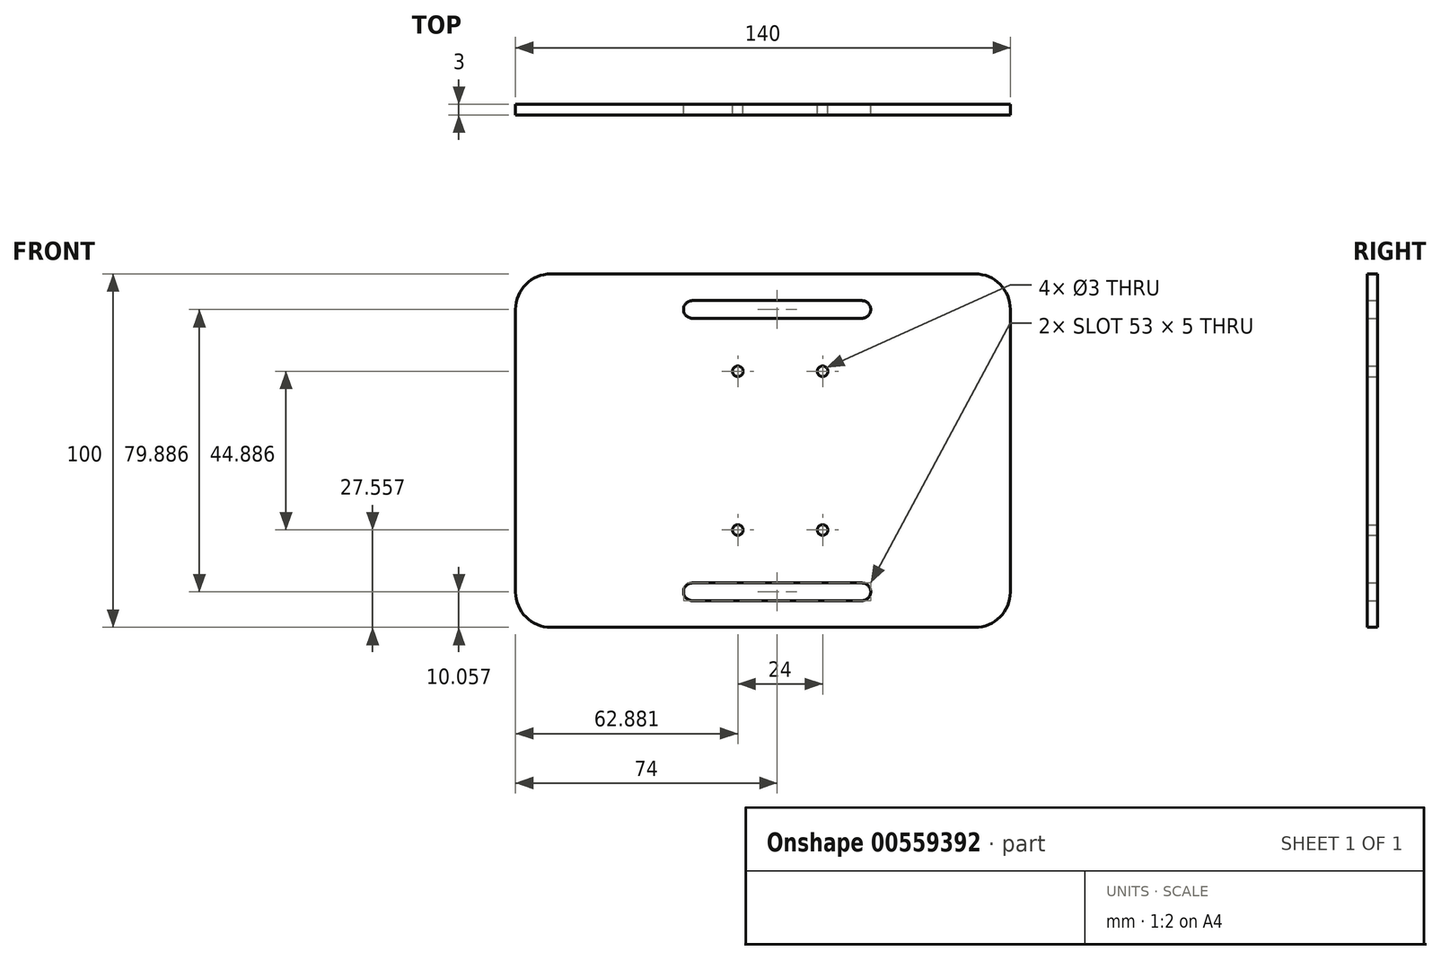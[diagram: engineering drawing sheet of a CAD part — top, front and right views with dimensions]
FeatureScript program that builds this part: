
annotation { "Feature Type Name" : "Feature", "Feature Type Description" : "" }
export const myFeature = defineFeature(function(context is Context, id is Id, definition is map)
    precondition{}
    {
        {
            var Q0;
            Q0=qCreatedBy(makeId("Front.planeOp"),FACE);
            var sketch = newSketch(context, id + "F0", { "sketchPlane" : qUnion([Q0])});
            skLineSegment(sketch, "E0.bottom", {"start": v(-140, 0) * mm, "end": v(0, 0) * mm});
            skLineSegment(sketch, "E0.top", {"start": v(-140, 50) * mm, "end": v(0, 50) * mm});
            skLineSegment(sketch, "E0.left", {"start": v(-140, 0) * mm, "end": v(-140, 50) * mm});
            skLineSegment(sketch, "E0.right", {"start": v(0, 0) * mm, "end": v(0, 50) * mm});
            skSolve(sketch);
        }
        {
            var Q0;
            Q0=qCreatedBy(makeId("Front.planeOp"),FACE);
            var sketch = newSketch(context, id + "F1", { "sketchPlane" : qUnion([Q0])});
            skLineSegment(sketch, "E1", {"start": v(-90, 39.94) * mm, "end": v(-42, 39.94) * mm});
            skArc(sketch, "E2.0.startCap", {"start": v(-90, 37.44) * mm, "mid": v(-92.5, 39.94) * mm, "end": v(-90, 42.44) * mm});
            skArc(sketch, "E2.0.endCap", {"start": v(-42, 42.44) * mm, "mid": v(-39.5, 39.94) * mm, "end": v(-42, 37.44) * mm});
            skLineSegment(sketch, "E2.0.left", {"start": v(-90, 42.44) * mm, "end": v(-42, 42.44) * mm});
            skLineSegment(sketch, "E2.0.right", {"start": v(-90, 37.44) * mm, "end": v(-42, 37.44) * mm});
            skSolve(sketch);
        }
        {
            var Q0;
            Q0=qCreatedBy(makeId("Front.planeOp"),FACE);
            var sketch = newSketch(context, id + "F2", { "sketchPlane" : qUnion([Q0])});
            skLineSegment(sketch, "E3", {"start": v(-77.12, 22.44) * mm, "end": v(-53.12, 22.44) * mm});
            skSolve(sketch);
        }
        {
            var Q0;
            Q0=qCreatedBy(makeId("Front.planeOp"),FACE);
            var sketch = newSketch(context, id + "F3", { "sketchPlane" : qUnion([Q0])});
            skSolve(sketch);
        }
        {
            var Q0;
            Q0=makeQuery(id+"F0.imprint","IMPRINT",FACE,{"disambiguationData":[TD([[makeQuery(id+"F0.imprint","IMPRINT",EDGE,{"derivedFrom":sQuery(id+"F0.wireOp",EDGE,"E0.bottom")}),1.0]])]});
            extrude(context, id + "F4", {"entities" : qUnion([Q0]), "depth" : 3 * mm, "offsetDistance" : 25 * mm});
        }
        {
            var Q0;
            Q0=sQuery(id+"F2.wireOp",VERTEX,"E3.end");
            var Q1;
            Q1=makeQuery(id+"F4.opExtrude","SWEPT_BODY",BODY,{"disambiguationData":[OSD([sQuery(id+"F0.wireOp",EDGE,"E0.bottom"),sQuery(id+"F0.wireOp",EDGE,"E0.top"),sQuery(id+"F0.wireOp",EDGE,"E0.left"),sQuery(id+"F0.wireOp",EDGE,"E0.right")])]});
            hole(context, id + "F5", {"style" : HoleStyle.SIMPLE, "endStyle" : HoleEndStyle.THROUGH, "oppositeDirection" : true, "holeDiameter" : 3 * mm, "isTappedThrough" : true, "tappedDepth" : 12 * mm, "tapClearance" : 3, "locations" : qUnion([Q0]), "scope" : qUnion([Q1])});
        }
        {
            var Q0;
            Q0=sQuery(id+"F2.wireOp",VERTEX,"E3.start");
            var Q1;
            Q1=makeQuery(id+"F4.opExtrude","SWEPT_BODY",BODY,{"disambiguationData":[OSD([sQuery(id+"F0.wireOp",EDGE,"E0.bottom"),sQuery(id+"F0.wireOp",EDGE,"E0.top"),sQuery(id+"F0.wireOp",EDGE,"E0.left"),sQuery(id+"F0.wireOp",EDGE,"E0.right")])]});
            hole(context, id + "F6", {"style" : HoleStyle.SIMPLE, "endStyle" : HoleEndStyle.THROUGH, "oppositeDirection" : true, "holeDiameter" : 3 * mm, "isTappedThrough" : true, "tappedDepth" : 12 * mm, "tapClearance" : 3, "locations" : qUnion([Q0]), "scope" : qUnion([Q1])});
        }
        {
            var Q0;
            Q0 = qSketchRegion(id + "F1", true);
            var sketch = newSketch(context, id + "F7", { "sketchPlane" : qUnion([Q0])});
            skSolve(sketch);
        }
        {
            var Q0;
            Q0 = qSketchRegion(id + "F1", true);
            extrude(context, id + "F8", {"entities" : qUnion([Q0]), "operationType" : NewBodyOperationType.REMOVE, "oppositeDirection" : true, "depth" : 25 * mm, "offsetDistance" : 25 * mm});
        }
        {
            var Q0;
            Q0 = qSketchRegion(id + "F1", true);
            extrude(context, id + "F9", {"entities" : qUnion([Q0]), "operationType" : NewBodyOperationType.REMOVE, "oppositeDirection" : true, "depth" : 25 * mm, "offsetDistance" : 25 * mm});
        }
        {
            var Q0;
            Q0 = qSketchRegion(id + "F1", true);
            var Q1;
            Q1=makeQuery(id+"F7.imprint","IMPRINT",FACE,{"disambiguationData":[TD([[makeQuery(id+"F7.imprint","IMPRINT",EDGE,{"derivedFrom":makeQuery(id+"F1.imprint","IMPRINT",EDGE,{"derivedFrom":sQuery(id+"F1.wireOp",EDGE,"E2.0.startCap")})}),-1.0]])]});
            extrude(context, id + "F10", {"entities" : qUnion([Q0, Q1]), "operationType" : NewBodyOperationType.REMOVE, "depth" : 15.43 * mm, "offsetDistance" : 25 * mm});
        }
        {
            var Q0;
            Q0=makeQuery(id+"F4.opExtrude","SWEPT_EDGE",EDGE,{"disambiguationData":[OSD([sQuery(id+"F0.wireOp",EDGE,"E0.top"),sQuery(id+"F0.wireOp",EDGE,"E0.right")])]});
            fillet(context, id + "F11", {"entities" : qUnion([Q0]), "radius" : 10 * mm, "tangentPropagation" : true, "allowEdgeOverflow" : false});
        }
        {
            var Q0;
            Q0=makeQuery(id+"F4.opExtrude","SWEPT_EDGE",EDGE,{"disambiguationData":[OSD([sQuery(id+"F0.wireOp",EDGE,"E0.top"),sQuery(id+"F0.wireOp",EDGE,"E0.left")])]});
            fillet(context, id + "F12", {"entities" : qUnion([Q0]), "radius" : 10 * mm, "tangentPropagation" : true, "allowEdgeOverflow" : false});
        }
        {
            var Q0;
            Q0=makeQuery(id+"F4.opExtrude","SWEPT_BODY",BODY,{"disambiguationData":[OSD([sQuery(id+"F0.wireOp",EDGE,"E0.bottom"),sQuery(id+"F0.wireOp",EDGE,"E0.top"),sQuery(id+"F0.wireOp",EDGE,"E0.left"),sQuery(id+"F0.wireOp",EDGE,"E0.right")])]});
            var Q1;
            Q1=qCreatedBy(makeId("Top.planeOp"),FACE);
            mirror(context, id + "F13", {"operationType" : NewBodyOperationType.ADD, "entities" : qUnion([Q0]), "mirrorPlane" : qUnion([Q1])});
        }
    });
